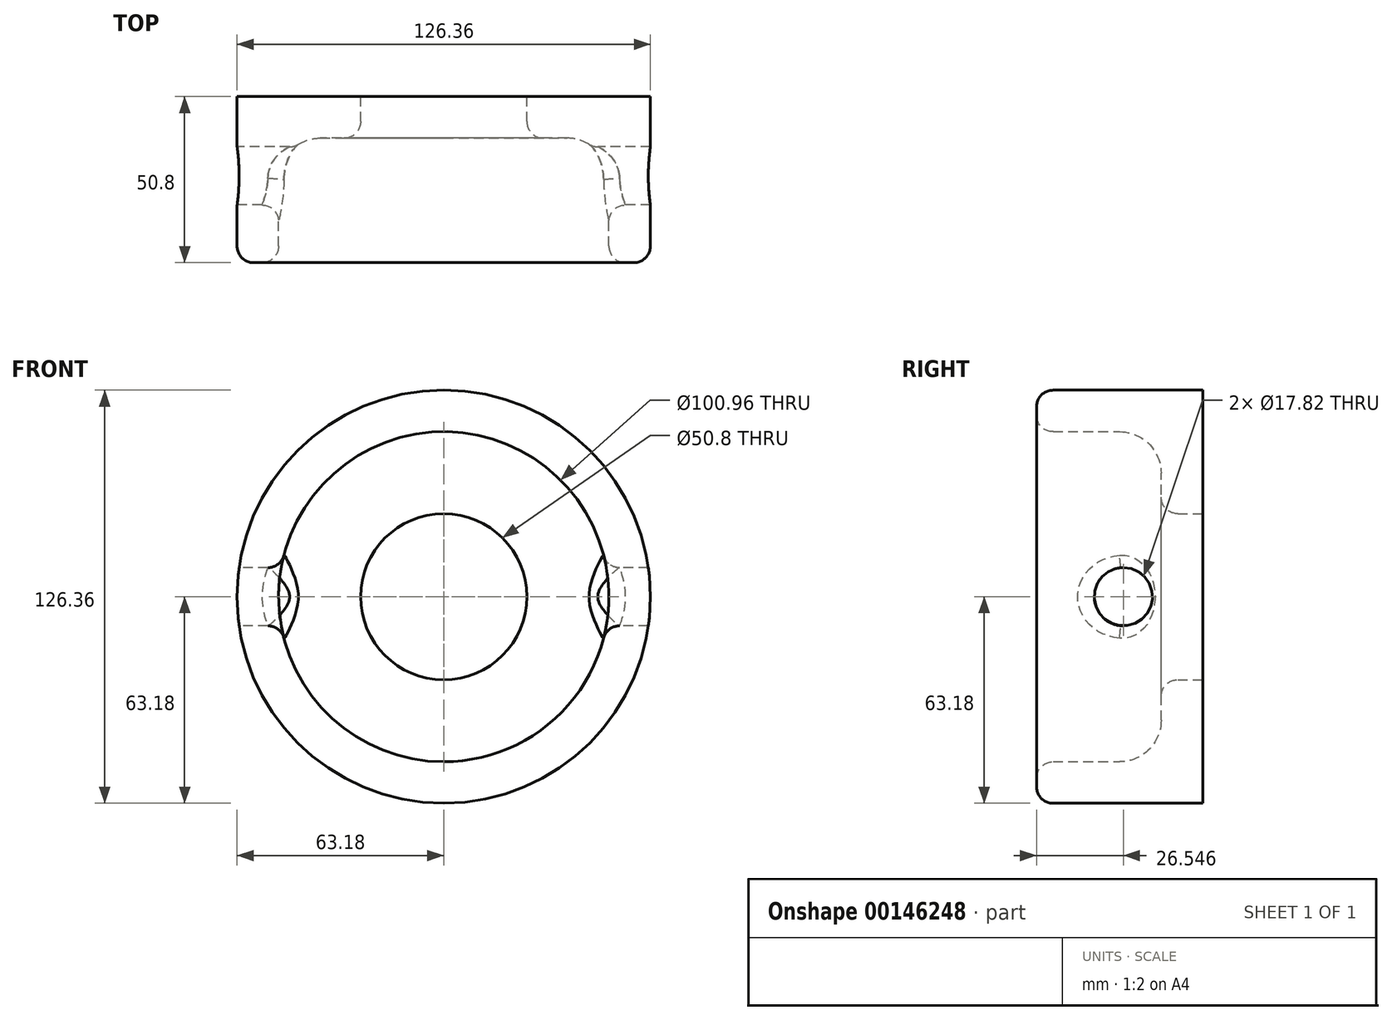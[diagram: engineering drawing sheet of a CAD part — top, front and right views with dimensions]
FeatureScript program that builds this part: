
annotation { "Feature Type Name" : "Feature", "Feature Type Description" : "" }
export const myFeature = defineFeature(function(context is Context, id is Id, definition is map)
    precondition{}
    {
        {
            var Q0;
            Q0=qCreatedBy(makeId("Front.planeOp"),FACE);
            var sketch = newSketch(context, id + "F9", { "sketchPlane" : qUnion([Q0])});
            skCircle(sketch, "E0", {"center": v(0, 0) * mm, "radius": 63.18 * mm});
            skSolve(sketch);
        }
        {
            var Q0;
            Q0 = qSketchRegion(id + "F9", true);
            extrude(context, id + "F10", {"entities" : qUnion([Q0]), "depth" : 50.8 * mm});
        }
        {
            var Q0;
            Q0=makeQuery(id+"F10.opExtrude","CAP_FACE",FACE,{"disambiguationData":[OSD([sQuery(id+"F9.wireOp",EDGE,"E0")])],"isStart":false});
            shell(context, id + "F0", {"entities" : qUnion([Q0]), "thickness" : 12.7 * mm});
        }
        {
            var Q0;
            Q0=qCreatedBy(makeId("Front.planeOp"),FACE);
            var sketch = newSketch(context, id + "F1", { "sketchPlane" : qUnion([Q0])});
            skCircle(sketch, "E1", {"center": v(0, 0) * mm, "radius": 25.4 * mm});
            skSolve(sketch);
        }
        {
            var Q0;
            Q0=makeQuery(id+"F1.imprint","IMPRINT",FACE,{"disambiguationData":[TD([[makeQuery(id+"F1.imprint","IMPRINT",EDGE,{"derivedFrom":sQuery(id+"F1.wireOp",EDGE,"E1")}),1.0]])]});
            extrude(context, id + "F2", {"entities" : qUnion([Q0]), "operationType" : NewBodyOperationType.REMOVE, "depth" : 41.54 * mm});
        }
        {
            var Q0;
            {var subQ0=sQuery(id+"F9.wireOp",EDGE,"E0");Q0=makeQuery(id+"F0.opShell","OFFSET_EDGE",EDGE,{"disambiguationData":[OSD([subQ0]),TDD([makeQuery(id+"F10.opExtrude","CAP_EDGE",EDGE,{"disambiguationData":[OSD([subQ0])],"isStart":true})])]});}
            fillet(context, id + "F3", {"entities" : qUnion([Q0]), "radius" : 12.7 * mm, "tangentPropagation" : true, "allowEdgeOverflow" : false});
        }
        {
            var Q0;
            {var subQ0=sQuery(id+"F9.wireOp",EDGE,"E0");Q0=makeQuery(id+"F2.boolean.opBoolean","INTERSECT",EDGE,{"derivedFrom":[makeQuery(id+"F0.opShell","OFFSET_FACE",FACE,{"disambiguationData":[OSD([subQ0]),TDD([makeQuery(id+"F10.opExtrude","CAP_FACE",FACE,{"disambiguationData":[OSD([subQ0])],"isStart":true})])]}),makeQuery(id+"F2.opExtrude","SWEPT_FACE",FACE,{"disambiguationData":[OSD([sQuery(id+"F1.wireOp",EDGE,"E1")])]})]});}
            fillet(context, id + "F11", {"entities" : qUnion([Q0]), "radius" : 5.08 * mm, "tangentPropagation" : true, "allowEdgeOverflow" : false});
        }
        {
            var Q0;
            {var subQ0=sQuery(id+"F9.wireOp",EDGE,"E0");Q0=makeQuery(id+"F0.opShell","OFFSET_EDGE",EDGE,{"disambiguationData":[OSD([subQ0]),TDD([makeQuery(id+"F10.opExtrude","CAP_EDGE",EDGE,{"disambiguationData":[OSD([subQ0])],"isStart":false})])]});}
            fillet(context, id + "F4", {"entities" : qUnion([Q0]), "radius" : 5.08 * mm, "tangentPropagation" : true, "allowEdgeOverflow" : false});
        }
        {
            var Q0;
            Q0=makeQuery(id+"F10.opExtrude","CAP_EDGE",EDGE,{"disambiguationData":[OSD([sQuery(id+"F9.wireOp",EDGE,"E0")])],"isStart":false});
            fillet(context, id + "F5", {"entities" : qUnion([Q0]), "radius" : 5.08 * mm, "tangentPropagation" : true, "allowEdgeOverflow" : false});
        }
        {
            var Q0;
            Q0=qCreatedBy(makeId("Right.planeOp"),FACE);
            var sketch = newSketch(context, id + "F6", { "sketchPlane" : qUnion([Q0])});
            skCircle(sketch, "E2", {"center": v(-24.25, 0) * mm, "radius": 8.9 * mm});
            skSolve(sketch);
        }
        {
            var Q0;
            Q0 = qSketchRegion(id + "F6", true);
            extrude(context, id + "F7", {"entities" : qUnion([Q0]), "operationType" : NewBodyOperationType.REMOVE, "depth" : 76.2 * mm, "hasSecondDirection" : true, "secondDirectionOppositeDirection" : true, "secondDirectionDepth" : 114.46 * mm});
        }
        {
            var Q0;
            Q0=makeQuery(id+"F7.boolean.opBoolean","INTERSECT",EDGE,{"disambiguationData":[OD(0.0)],"derivedFrom":[makeQuery(id+"F3.opFillet","BLEND_FACE",FACE,{"disambiguationData":[OSD([sQuery(id+"F9.wireOp",EDGE,"E0")])]}),makeQuery(id+"F7.opExtrude","SWEPT_FACE",FACE,{"disambiguationData":[OSD([sQuery(id+"F6.wireOp",EDGE,"E2")])]})]});
            var Q1;
            {var subQ0=sQuery(id+"F9.wireOp",EDGE,"E0");Q1=makeQuery(id+"F7.boolean.opBoolean","INTERSECT",EDGE,{"disambiguationData":[OD(0.0)],"derivedFrom":[makeQuery(id+"F0.opShell","OFFSET_FACE",FACE,{"disambiguationData":[OSD([subQ0]),TDD([makeQuery(id+"F10.opExtrude","SWEPT_FACE",FACE,{"disambiguationData":[OSD([subQ0])]})])]}),makeQuery(id+"F7.opExtrude","SWEPT_FACE",FACE,{"disambiguationData":[OSD([sQuery(id+"F6.wireOp",EDGE,"E2")])]})]});}
            fillet(context, id + "F8", {"entities" : qUnion([Q0, Q1]), "radius" : 5.08 * mm, "tangentPropagation" : true, "allowEdgeOverflow" : false});
        }
        {
            var Q0;
            {var subQ0=sQuery(id+"F9.wireOp",EDGE,"E0");Q0=makeQuery(id+"F7.boolean.opBoolean","INTERSECT",EDGE,{"disambiguationData":[OD(1.0)],"derivedFrom":[makeQuery(id+"F0.opShell","OFFSET_FACE",FACE,{"disambiguationData":[OSD([subQ0]),TDD([makeQuery(id+"F10.opExtrude","SWEPT_FACE",FACE,{"disambiguationData":[OSD([subQ0])]})])]}),makeQuery(id+"F7.opExtrude","SWEPT_FACE",FACE,{"disambiguationData":[OSD([sQuery(id+"F6.wireOp",EDGE,"E2")])]})]});}
            var Q1;
            Q1=makeQuery(id+"F7.boolean.opBoolean","INTERSECT",EDGE,{"disambiguationData":[OD(1.0)],"derivedFrom":[makeQuery(id+"F3.opFillet","BLEND_FACE",FACE,{"disambiguationData":[OSD([sQuery(id+"F9.wireOp",EDGE,"E0")])]}),makeQuery(id+"F7.opExtrude","SWEPT_FACE",FACE,{"disambiguationData":[OSD([sQuery(id+"F6.wireOp",EDGE,"E2")])]})]});
            fillet(context, id + "F12", {"entities" : qUnion([Q0, Q1]), "radius" : 5.08 * mm, "tangentPropagation" : true, "allowEdgeOverflow" : false});
        }
    });
